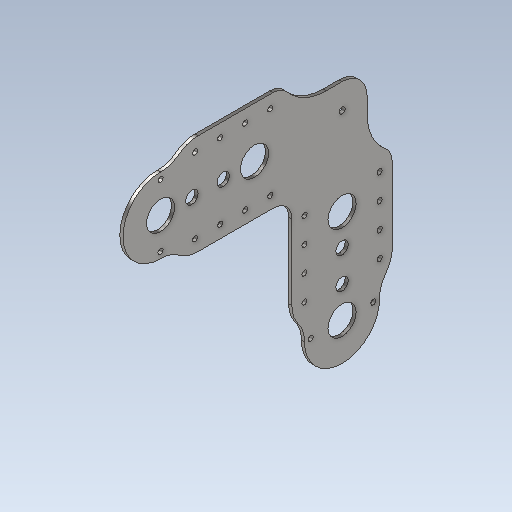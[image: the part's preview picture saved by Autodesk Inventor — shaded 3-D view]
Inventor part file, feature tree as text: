
AUTODESK INVENTOR PART (.ipt)
format: ipt  version: 2023 (Build 270158000, 158)  size: 235,008 bytes
history: native  units: in
note: dims shown in document units (in); Inventor stores cm internally (conversion verified against a paired STEP export)
features: fillet x3, extrude x1
ambient origin geometry x8: Origin, YZ Plane, XZ Plane, XY Plane, X Axis, Y Axis, Z Axis, Center Point
bodies: Solid1 (feature_tree)
feature tree (4):
  extrude  "Extrusion1"  Depth=4.0in
  fillet  "Fillet1"  Radius=6.0in
  fillet  "Fillet2"  Radius=1.125in
  fillet  "Fillet3"  Radius=0.5in
